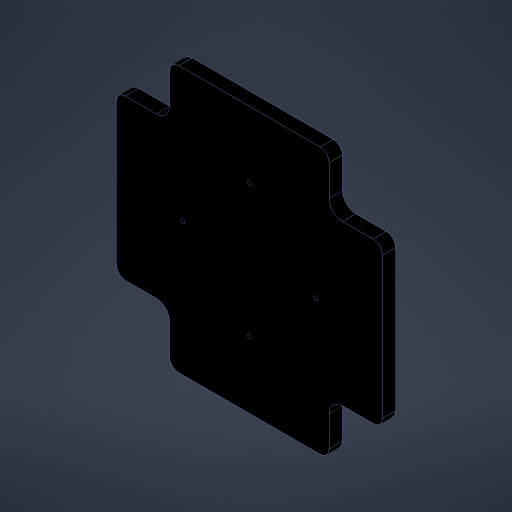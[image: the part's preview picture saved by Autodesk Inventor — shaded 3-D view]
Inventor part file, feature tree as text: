
AUTODESK INVENTOR PART (.ipt)
format: ipt  version: 2023 (Build 270158000, 158)  size: 240,128 bytes
history: native  units: mm
features: fillet x3, extrude x1, direct_edit x1, other x1
ambient origin geometry x8: Origin, YZ Plane, XZ Plane, XY Plane, X Axis, Y Axis, Z Axis, Center Point
bodies: Solid1 (feature_tree)
feature tree (6):
  extrude  "Extrusion1"  Depth=200.0mm
  fillet  "Fillet1"  Radius=200.0mm
  fillet  "Fillet2"  Radius=40.0mm
  fillet  "Fillet3"  Radius=40.0mm
  direct_edit  "Direct Edit2"
  other  "Scale2"
